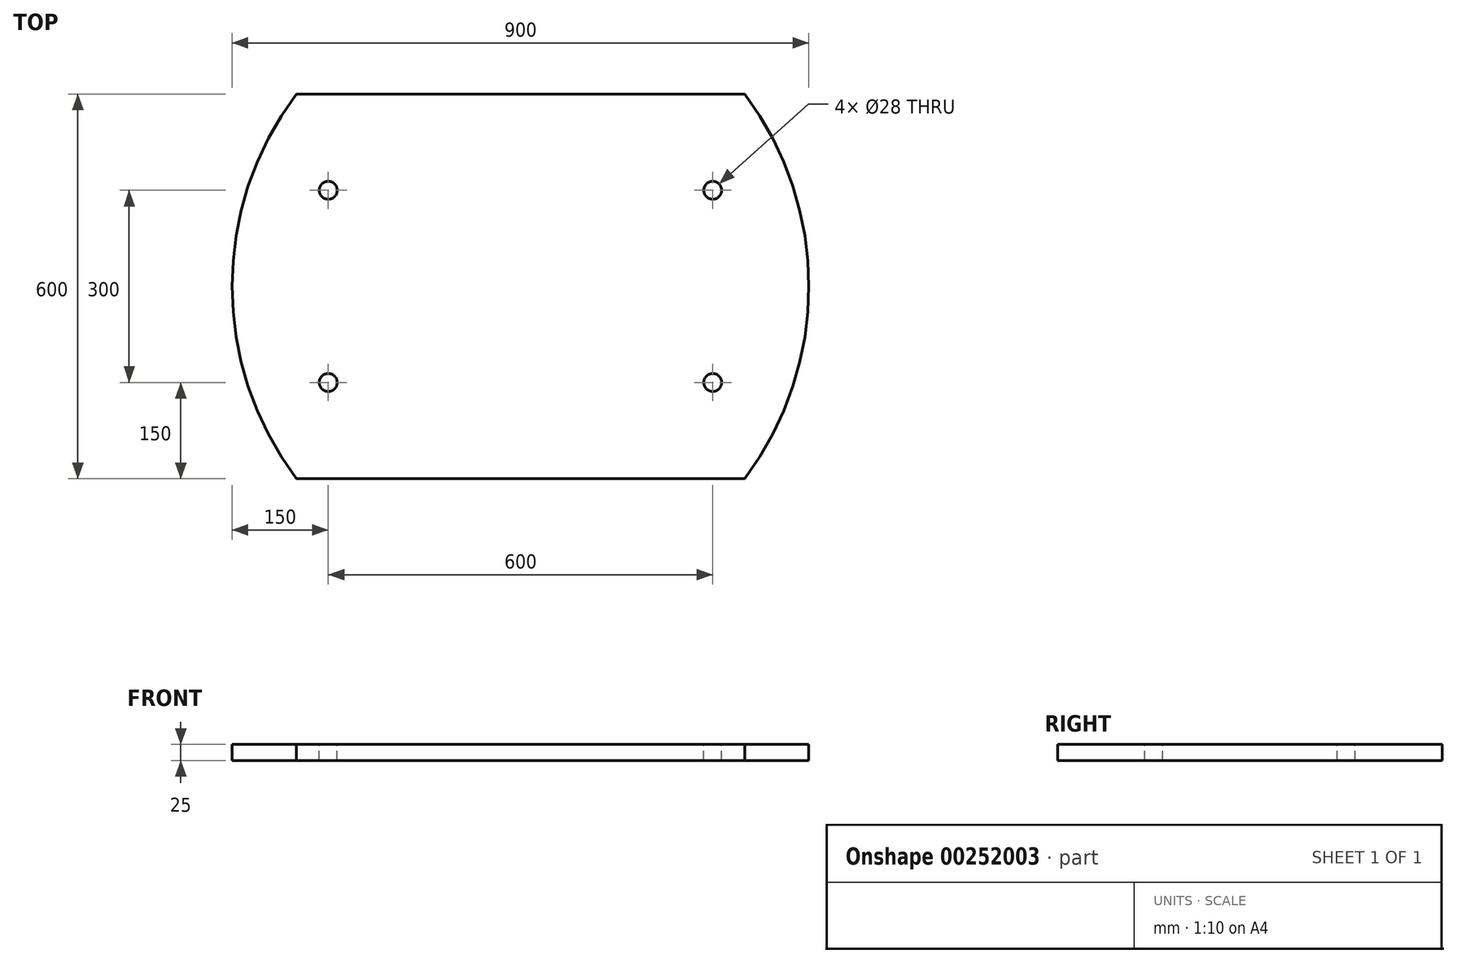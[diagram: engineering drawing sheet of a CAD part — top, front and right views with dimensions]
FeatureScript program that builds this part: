
annotation { "Feature Type Name" : "Feature", "Feature Type Description" : "" }
export const myFeature = defineFeature(function(context is Context, id is Id, definition is map)
    precondition{}
    {
        {
            var Q0;
            Q0=qCreatedBy(makeId("Top.planeOp"),FACE);
            var sketch = newSketch(context, id + "F0", { "sketchPlane" : qUnion([Q0])});
            skLineSegment(sketch, "E0", {"start": v(-350, 300) * mm, "end": v(350, 300) * mm});
            skLineSegment(sketch, "E1", {"start": v(-350, -300) * mm, "end": v(350, -300) * mm});
            skCircle(sketch, "E2", {"center": v(0, 0) * mm, "radius": 250 * mm});
            skArc(sketch, "E3", {"start": v(-350, 300) * mm, "mid": v(-450, 0) * mm, "end": v(-350, -300) * mm});
            skArc(sketch, "E4", {"start": v(350, -300) * mm, "mid": v(450, 0) * mm, "end": v(350, 300) * mm});
            skCircle(sketch, "E5", {"center": v(-300, 150) * mm, "radius": 14 * mm});
            skCircle(sketch, "E6", {"center": v(300, 150) * mm, "radius": 14 * mm});
            skCircle(sketch, "E7", {"center": v(-300, -150) * mm, "radius": 14 * mm});
            skCircle(sketch, "E8", {"center": v(300, -150) * mm, "radius": 14 * mm});
            skSolve(sketch);
        }
        {
            var Q0;
            Q0=makeQuery(id+"F0.imprint","IMPRINT",FACE,{"disambiguationData":[TD([[makeQuery(id+"F0.imprint","IMPRINT",EDGE,{"derivedFrom":sQuery(id+"F0.wireOp",EDGE,"E0")}),-1.0]])]});
            var Q1;
            Q1=makeQuery(id+"F0.imprint","IMPRINT",FACE,{"disambiguationData":[TD([[makeQuery(id+"F0.imprint","IMPRINT",EDGE,{"derivedFrom":sQuery(id+"F0.wireOp",EDGE,"E2")}),1.0]])]});
            extrude(context, id + "F1", {"entities" : qUnion([Q0, Q1]), "oppositeDirection" : true, "depth" : 25 * mm});
        }
    });
